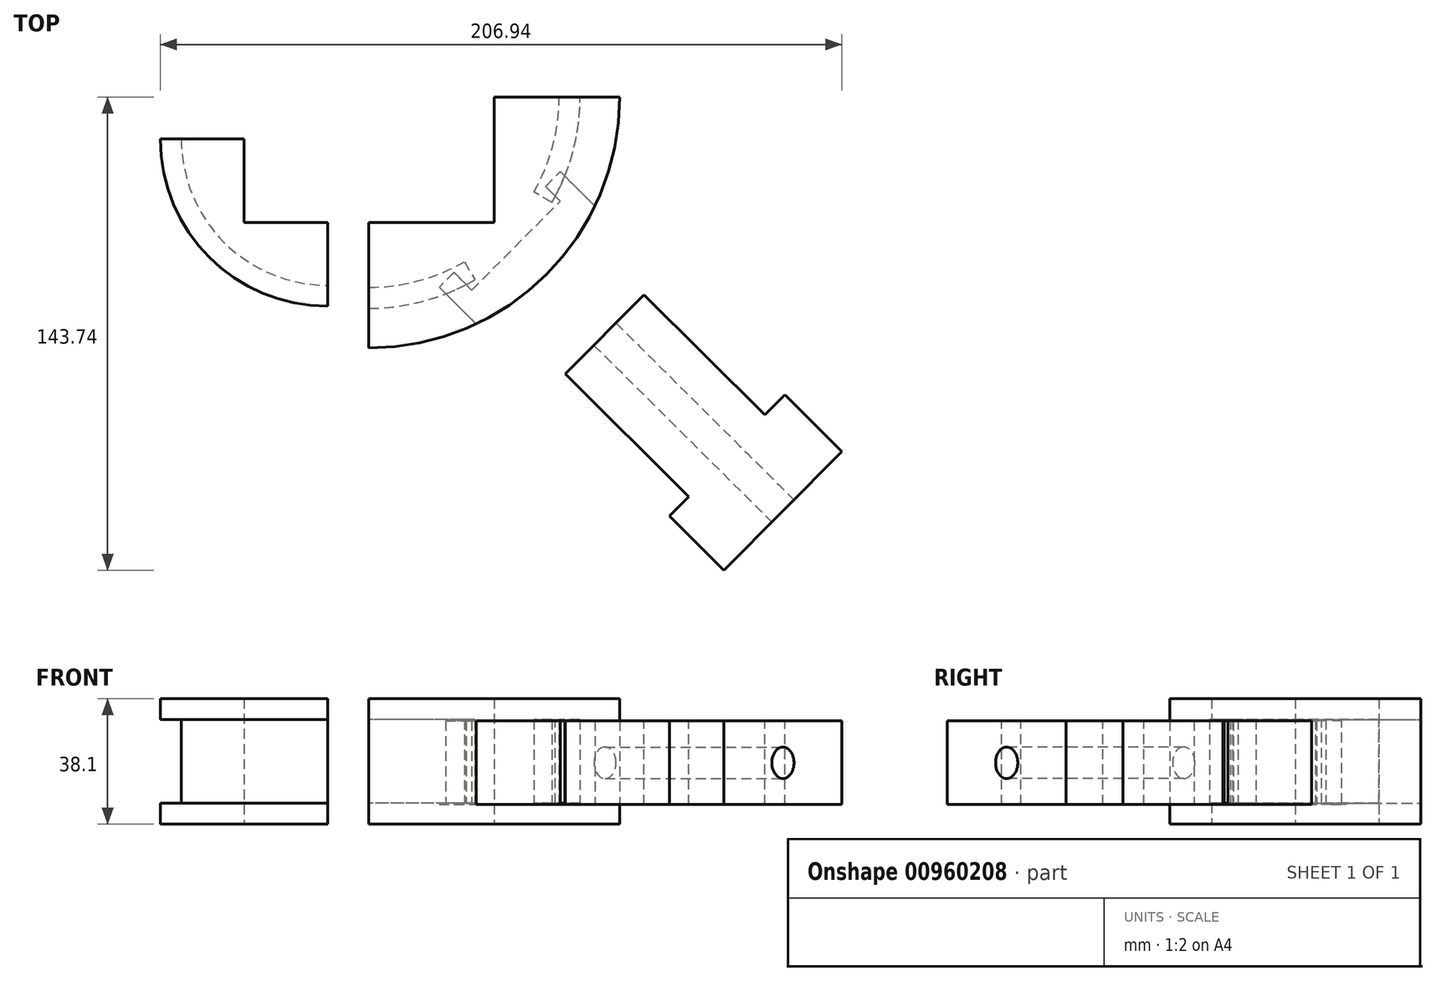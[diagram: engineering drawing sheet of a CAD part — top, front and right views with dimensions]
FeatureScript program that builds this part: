
annotation { "Feature Type Name" : "Feature", "Feature Type Description" : "" }
export const myFeature = defineFeature(function(context is Context, id is Id, definition is map)
    precondition{}
    {
        {
            var Q0;
            Q0=qCreatedBy(makeId("Top.planeOp"),FACE);
            var sketch = newSketch(context, id + "F0", { "sketchPlane" : qUnion([Q0])});
            skLineSegment(sketch, "E0.bottom", {"start": v(-25.4, 25.4) * mm, "end": v(0, 25.4) * mm});
            skLineSegment(sketch, "E0.right", {"start": v(25.4, 0) * mm, "end": v(25.4, -25.4) * mm});
            skPoint(sketch, "E0.middle", {"position": v(0, 0) * mm});
            skLineSegment(sketch, "E1", {"start": v(0, 25.4) * mm, "end": v(0, 0) * mm});
            skLineSegment(sketch, "E2", {"start": v(25.4, 0) * mm, "end": v(0, 0) * mm});
            skPoint(sketch, "E3.orphan", {"position": v(25.4, 25.4) * mm});
            skArc(sketch, "E4", {"start": v(-25.4, 25.4) * mm, "mid": v(-10.52, -10.52) * mm, "end": v(25.4, -25.4) * mm});
            skPoint(sketch, "E0.top.start.orphan", {"position": v(-25.4, -25.4) * mm});
            skSolve(sketch);
        }
        {
            var Q0;
            Q0=makeQuery(id+"F0.imprint","IMPRINT",FACE,{"disambiguationData":[TD([[makeQuery(id+"F0.imprint","IMPRINT",EDGE,{"derivedFrom":sQuery(id+"F0.wireOp",EDGE,"E0.bottom")}),-1.0]])]});
            extrude(context, id + "F1", {"entities" : qUnion([Q0]), "depth" : 38.1 * mm, "offsetDistance" : 25.4 * mm});
        }
        {
            var Q0;
            Q0=makeQuery(id+"F1.opExtrude","SWEPT_FACE",FACE,{"disambiguationData":[OSD([sQuery(id+"F0.wireOp",EDGE,"E0.right")])]});
            var sketch = newSketch(context, id + "F2", { "sketchPlane" : qUnion([Q0])});
            skLineSegment(sketch, "E5", {"start": v(25.37, 0) * mm, "end": v(25.37, 50.85) * mm, "construction": true});
            skLineSegment(sketch, "E6.bottom", {"start": v(-31.75, 31.75) * mm, "end": v(-19.05, 31.75) * mm});
            skLineSegment(sketch, "E6.top", {"start": v(-31.75, 6.35) * mm, "end": v(-19.05, 6.35) * mm});
            skLineSegment(sketch, "E6.left", {"start": v(-31.75, 31.75) * mm, "end": v(-31.75, 6.35) * mm});
            skLineSegment(sketch, "E6.right", {"start": v(-19.05, 31.75) * mm, "end": v(-19.05, 6.35) * mm});
            skPoint(sketch, "E6.middle", {"position": v(-25.4, 19.05) * mm});
            skSolve(sketch);
        }
        {
            var Q0;
            {var subQ0=sQuery(id+"F2.wireOp",EDGE,"lC9828bi-HIS0-zRGc-7378-FjSk739L89TA.left");Q0=makeQuery(id+"F2.imprint","IMPRINT",FACE,{"disambiguationData":[TD([[makeQuery(id+"F2.imprint","IMPRINT",EDGE,{"derivedFrom":subQ0}),1.0]])]});}
            var Q1;
            {var subQ0=sQuery(id+"F2.wireOp",EDGE,"E6.left");Q1=makeQuery(id+"F2.imprint","IMPRINT",FACE,{"disambiguationData":[TD([[makeQuery(id+"F2.imprint","IMPRINT",EDGE,{"derivedFrom":subQ0}),1.0]])]});}
            var Q2;
            {var subQ0=sQuery(id+"F2.wireOp",EDGE,"E6.right");Q2=makeQuery(id+"F2.imprint","IMPRINT",FACE,{"disambiguationData":[TD([[makeQuery(id+"F2.imprint","IMPRINT",EDGE,{"derivedFrom":subQ0}),-1.0]])]});}
            var Q3;
            Q3=sQuery(id+"F2.wireOp",EDGE,"E5");
            revolve(context, id + "F3", {"operationType" : NewBodyOperationType.REMOVE, "surfaceOperationType" : NewSurfaceOperationType.NEW, "entities" : qUnion([Q0, Q1, Q2]), "axis" : qUnion([Q3]), "revolveType" : RevolveType.ONE_DIRECTION, "oppositeDirection" : true, "angle" : 91 * degree});
        }
        {
            var Q0;
            Q0=qCreatedBy(makeId("Top.planeOp"),FACE);
            var sketch = newSketch(context, id + "F4", { "sketchPlane" : qUnion([Q0])});
            skLineSegment(sketch, "E7.bottom", {"start": v(76, 38.1) * mm, "end": v(114.1, 38.1) * mm});
            skLineSegment(sketch, "E7.left", {"start": v(37.9, 0) * mm, "end": v(37.9, -38.1) * mm});
            skPoint(sketch, "E7.middle", {"position": v(76, 0) * mm});
            skLineSegment(sketch, "E8", {"start": v(-25.65, 0) * mm, "end": v(-25.65, 94.86) * mm, "construction": true});
            skLineSegment(sketch, "E9", {"start": v(76, 38.1) * mm, "end": v(76, 0) * mm});
            skLineSegment(sketch, "E10", {"start": v(76, 0) * mm, "end": v(37.9, 0) * mm});
            skPoint(sketch, "E11.orphan", {"position": v(37.9, 38.1) * mm});
            skArc(sketch, "E12", {"start": v(37.9, -38.1) * mm, "mid": v(91.8, -15.78) * mm, "end": v(114.1, 38.1) * mm});
            skPoint(sketch, "E7.right.end.orphan", {"position": v(114.1, -38.1) * mm});
            skSolve(sketch);
        }
        {
            var Q0;
            Q0=makeQuery(id+"F4.imprint","IMPRINT",FACE,{"disambiguationData":[TD([[makeQuery(id+"F4.imprint","IMPRINT",EDGE,{"derivedFrom":sQuery(id+"F4.wireOp",EDGE,"E7.bottom")}),-1.0]])]});
            extrude(context, id + "F5", {"entities" : qUnion([Q0]), "depth" : 38.1 * mm, "offsetDistance" : 25.4 * mm});
        }
        {
            var Q0;
            Q0=makeQuery(id+"F5.opExtrude","SWEPT_FACE",FACE,{"disambiguationData":[OSD([sQuery(id+"F4.wireOp",EDGE,"E7.left")])]});
            var sketch = newSketch(context, id + "F6", { "sketchPlane" : qUnion([Q0])});
            skLineSegment(sketch, "E13.bottom", {"start": v(19.69, 31.75) * mm, "end": v(26.04, 31.75) * mm});
            skLineSegment(sketch, "E13.top", {"start": v(19.69, 6.35) * mm, "end": v(26.04, 6.35) * mm});
            skLineSegment(sketch, "E13.left", {"start": v(19.69, 31.75) * mm, "end": v(19.69, 6.35) * mm});
            skLineSegment(sketch, "E13.right", {"start": v(26.04, 31.75) * mm, "end": v(26.04, 6.35) * mm});
            skPoint(sketch, "E13.middle", {"position": v(22.86, 19.05) * mm});
            skLineSegment(sketch, "E14", {"start": v(-38.3, 0) * mm, "end": v(-38.3, 66.4) * mm, "construction": true});
            skSolve(sketch);
        }
        {
            var Q0;
            Q0=makeQuery(id+"F6.imprint","IMPRINT",FACE,{"disambiguationData":[TD([[makeQuery(id+"F6.imprint","IMPRINT",EDGE,{"derivedFrom":sQuery(id+"F6.wireOp",EDGE,"E13.bottom")}),-1.0]])]});
            var Q1;
            Q1=sQuery(id+"F6.wireOp",EDGE,"E14");
            revolve(context, id + "F7", {"operationType" : NewBodyOperationType.REMOVE, "surfaceOperationType" : NewSurfaceOperationType.NEW, "entities" : qUnion([Q0]), "axis" : qUnion([Q1]), "revolveType" : RevolveType.ONE_DIRECTION, "angle" : 30 * degree});
        }
        {
            var Q0;
            Q0=makeQuery(id+"F5.opExtrude","SWEPT_FACE",FACE,{"disambiguationData":[OSD([sQuery(id+"F4.wireOp",EDGE,"E7.bottom")])]});
            var sketch = newSketch(context, id + "F8", { "sketchPlane" : qUnion([Q0])});
            skLineSegment(sketch, "E15.bottom", {"start": v(-102.04, 31.75) * mm, "end": v(-95.7, 31.75) * mm});
            skLineSegment(sketch, "E15.top", {"start": v(-102.04, 6.35) * mm, "end": v(-95.7, 6.35) * mm});
            skLineSegment(sketch, "E15.left", {"start": v(-102.04, 31.75) * mm, "end": v(-102.04, 6.35) * mm});
            skLineSegment(sketch, "E15.right", {"start": v(-95.7, 31.75) * mm, "end": v(-95.7, 6.35) * mm});
            skPoint(sketch, "E15.middle", {"position": v(-98.87, 19.05) * mm});
            skLineSegment(sketch, "E16", {"start": v(-38.1, 0) * mm, "end": v(-38.1, 56.54) * mm, "construction": true});
            skSolve(sketch);
        }
        {
            var Q0;
            Q0=makeQuery(id+"F5.opExtrude","SWEPT_FACE",FACE,{"disambiguationData":[OSD([sQuery(id+"F4.wireOp",EDGE,"E12")])]});
            var Q1;
            Q1=qCreatedBy(makeId("Origin.pointOp"),VERTEX);
            cPlane(context, id + "F9", {"entities" : qUnion([Q0, Q1]), "cplaneType" : CPlaneType.LINE_ANGLE, "offset" : 25.4 * mm, "angle" : 180 * degree, "width" : 152.4 * mm, "height" : 152.4 * mm});
        }
        {
            var Q0;
            Q0=qCreatedBy(id+"F9.planeOp",FACE);
            cPlane(context, id + "F10", {"entities" : qUnion([Q0]), "cplaneType" : CPlaneType.OFFSET, "offset" : 101.6 * mm, "width" : 152.4 * mm, "height" : 152.4 * mm});
        }
        {
            var Q0;
            Q0=qCreatedBy(id+"F10.planeOp",FACE);
            var sketch = newSketch(context, id + "F11", { "sketchPlane" : qUnion([Q0])});
            skLineSegment(sketch, "E17.bottom", {"start": v(27.89, 31.32) * mm, "end": v(78.69, 31.32) * mm});
            skLineSegment(sketch, "E17.top", {"start": v(27.89, 5.92) * mm, "end": v(78.69, 5.92) * mm});
            skLineSegment(sketch, "E17.left", {"start": v(27.89, 31.32) * mm, "end": v(27.89, 5.92) * mm});
            skLineSegment(sketch, "E17.right", {"start": v(78.69, 31.32) * mm, "end": v(78.69, 5.92) * mm});
            skPoint(sketch, "E17.middle", {"position": v(53.29, 18.62) * mm});
            skSolve(sketch);
        }
        {
            var Q0;
            Q0=makeQuery(id+"F11.imprint","IMPRINT",FACE,{"disambiguationData":[TD([[makeQuery(id+"F11.imprint","IMPRINT",EDGE,{"derivedFrom":sQuery(id+"F11.wireOp",EDGE,"E17.bottom")}),-1.0]])]});
            extrude(context, id + "F12", {"entities" : qUnion([Q0]), "operationType" : NewBodyOperationType.REMOVE, "oppositeDirection" : true, "depth" : 38.1 * mm, "offsetDistance" : 25.4 * mm});
        }
        {
            var Q0;
            Q0=makeQuery(id+"F8.imprint","IMPRINT",FACE,{"disambiguationData":[TD([[makeQuery(id+"F8.imprint","IMPRINT",EDGE,{"derivedFrom":sQuery(id+"F8.wireOp",EDGE,"E15.bottom")}),-1.0]])]});
            var Q1;
            Q1=sQuery(id+"F8.wireOp",EDGE,"E16");
            revolve(context, id + "F13", {"operationType" : NewBodyOperationType.REMOVE, "surfaceOperationType" : NewSurfaceOperationType.NEW, "entities" : qUnion([Q0]), "axis" : qUnion([Q1]), "revolveType" : RevolveType.ONE_DIRECTION, "oppositeDirection" : true, "angle" : 30 * degree});
        }
        {
            var Q0;
            Q0=makeQuery(id+"F12.boolean.opBoolean","COPY",FACE,{"derivedFrom":makeQuery(id+"F12.opExtrude","CAP_FACE",FACE,{"disambiguationData":[OSD([sQuery(id+"F11.wireOp",EDGE,"E17.bottom"),sQuery(id+"F11.wireOp",EDGE,"E17.top"),sQuery(id+"F11.wireOp",EDGE,"E17.left"),sQuery(id+"F11.wireOp",EDGE,"E17.right")])],"isStart":false})});
            var sketch = newSketch(context, id + "F14", { "sketchPlane" : qUnion([Q0])});
            skLineSegment(sketch, "E18.bottom", {"start": v(27.89, 31.32) * mm, "end": v(34.24, 31.32) * mm});
            skLineSegment(sketch, "E18.top", {"start": v(27.89, 5.92) * mm, "end": v(34.24, 5.92) * mm});
            skLineSegment(sketch, "E18.left", {"start": v(27.89, 31.32) * mm, "end": v(27.89, 5.92) * mm});
            skLineSegment(sketch, "E18.right", {"start": v(34.24, 31.32) * mm, "end": v(34.24, 5.92) * mm});
            skSolve(sketch);
        }
        {
            var Q0;
            Q0=makeQuery(id+"F14.imprint","IMPRINT",FACE,{"disambiguationData":[TD([[makeQuery(id+"F14.imprint","IMPRINT",EDGE,{"derivedFrom":sQuery(id+"F14.wireOp",EDGE,"E18.bottom")}),-1.0]])]});
            extrude(context, id + "F15", {"entities" : qUnion([Q0]), "operationType" : NewBodyOperationType.REMOVE, "oppositeDirection" : true, "depth" : 7.62 * mm, "offsetDistance" : 25.4 * mm});
        }
        {
            var Q0;
            Q0=makeQuery(id+"F12.boolean.opBoolean","COPY",FACE,{"derivedFrom":makeQuery(id+"F12.opExtrude","CAP_FACE",FACE,{"disambiguationData":[OSD([sQuery(id+"F11.wireOp",EDGE,"E17.bottom"),sQuery(id+"F11.wireOp",EDGE,"E17.top"),sQuery(id+"F11.wireOp",EDGE,"E17.left"),sQuery(id+"F11.wireOp",EDGE,"E17.right")])],"isStart":false})});
            var sketch = newSketch(context, id + "F16", { "sketchPlane" : qUnion([Q0])});
            skLineSegment(sketch, "E19.bottom", {"start": v(78.69, 31.32) * mm, "end": v(72.34, 31.32) * mm});
            skLineSegment(sketch, "E19.top", {"start": v(78.69, 5.92) * mm, "end": v(72.34, 5.92) * mm});
            skLineSegment(sketch, "E19.left", {"start": v(78.69, 31.32) * mm, "end": v(78.69, 5.92) * mm});
            skLineSegment(sketch, "E19.right", {"start": v(72.34, 31.32) * mm, "end": v(72.34, 5.92) * mm});
            skSolve(sketch);
        }
        {
            var Q0;
            Q0=makeQuery(id+"F16.imprint","IMPRINT",FACE,{"disambiguationData":[TD([[makeQuery(id+"F16.imprint","IMPRINT",EDGE,{"derivedFrom":sQuery(id+"F16.wireOp",EDGE,"E19.bottom")}),-1.0]])]});
            extrude(context, id + "F17", {"entities" : qUnion([Q0]), "operationType" : NewBodyOperationType.REMOVE, "oppositeDirection" : true, "depth" : 6.35 * mm, "offsetDistance" : 25.4 * mm});
        }
        {
            var Q0;
            Q0=makeQuery(id+"F11.imprint","IMPRINT",FACE,{"disambiguationData":[TD([[makeQuery(id+"F11.imprint","IMPRINT",EDGE,{"derivedFrom":sQuery(id+"F11.wireOp",EDGE,"E17.bottom")}),-1.0]])]});
            extrude(context, id + "F18", {"entities" : qUnion([Q0]), "depth" : 76.2 * mm, "offsetDistance" : 25.4 * mm});
        }
        {
            var Q0;
            Q0=makeQuery(id+"F18.opExtrude","CAP_FACE",FACE,{"disambiguationData":[OSD([sQuery(id+"F11.wireOp",EDGE,"E17.bottom"),sQuery(id+"F11.wireOp",EDGE,"E17.top"),sQuery(id+"F11.wireOp",EDGE,"E17.left"),sQuery(id+"F11.wireOp",EDGE,"E17.right")])],"isStart":false});
            var sketch = newSketch(context, id + "F19", { "sketchPlane" : qUnion([Q0])});
            skCircle(sketch, "E20", {"center": v(53.29, 18.62) * mm, "radius": 4.76 * mm});
            skPoint(sketch, "E20.centerSnap0", {"position": v(27.89, 18.62) * mm});
            skSolve(sketch);
        }
        {
            var Q0;
            Q0=makeQuery(id+"F19.imprint","IMPRINT",FACE,{"disambiguationData":[TD([[makeQuery(id+"F19.imprint","IMPRINT",EDGE,{"derivedFrom":sQuery(id+"F19.wireOp",EDGE,"E20")}),1.0]])]});
            extrude(context, id + "F20", {"entities" : qUnion([Q0]), "operationType" : NewBodyOperationType.REMOVE, "oppositeDirection" : true, "depth" : 76.2 * mm, "offsetDistance" : 25.4 * mm});
        }
        {
            var Q0;
            Q0=makeQuery(id+"F18.opExtrude","SWEPT_FACE",FACE,{"disambiguationData":[OSD([sQuery(id+"F11.wireOp",EDGE,"E17.bottom")])]});
            var sketch = newSketch(context, id + "F21", { "sketchPlane" : qUnion([Q0])});
            skLineSegment(sketch, "E21", {"start": v(97.57, -45.99) * mm, "end": v(135.04, -83.27) * mm});
            skLineSegment(sketch, "E22", {"start": v(135.04, -83.27) * mm, "end": v(129.16, -89.18) * mm});
            skLineSegment(sketch, "E23", {"start": v(121.48, -21.96) * mm, "end": v(158.13, -58.43) * mm});
            skLineSegment(sketch, "E24", {"start": v(158.13, -58.43) * mm, "end": v(164.63, -51.9) * mm});
            skSolve(sketch);
        }
        {
            var Q0;
            {var subQ0=sQuery(id+"F21.wireOp",EDGE,"E21");Q0=makeQuery(id+"F21.imprint","IMPRINT",FACE,{"disambiguationData":[TD([[makeQuery(id+"F21.imprint","IMPRINT",EDGE,{"derivedFrom":subQ0}),-1.0]])]});}
            var Q1;
            {var subQ0=sQuery(id+"F21.wireOp",EDGE,"E23");Q1=makeQuery(id+"F21.imprint","IMPRINT",FACE,{"disambiguationData":[TD([[makeQuery(id+"F21.imprint","IMPRINT",EDGE,{"derivedFrom":subQ0}),1.0]])]});}
            extrude(context, id + "F22", {"entities" : qUnion([Q0, Q1]), "operationType" : NewBodyOperationType.REMOVE, "oppositeDirection" : true, "depth" : 25.4 * mm, "offsetDistance" : 25.4 * mm});
        }
    });
